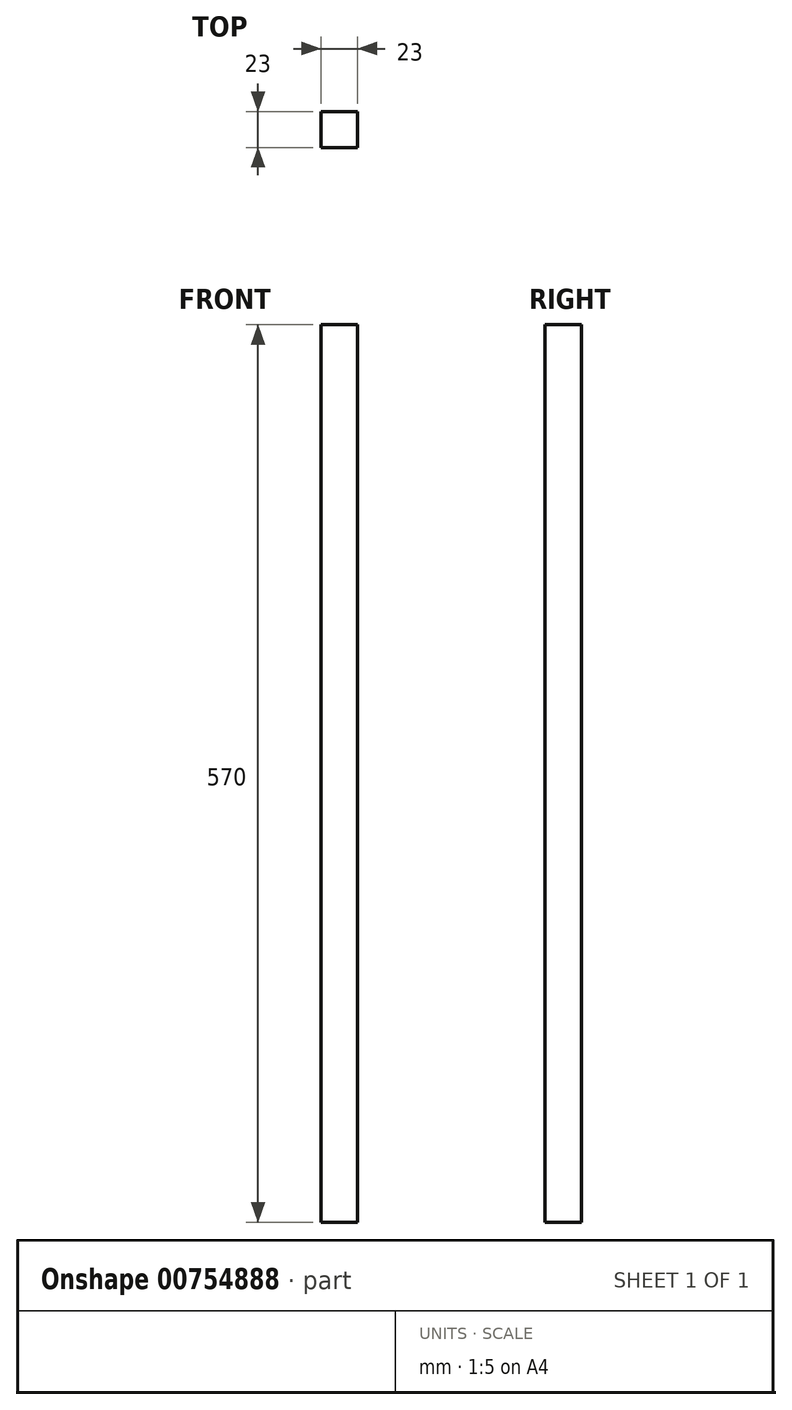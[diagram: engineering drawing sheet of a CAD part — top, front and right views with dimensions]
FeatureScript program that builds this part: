
annotation { "Feature Type Name" : "Feature", "Feature Type Description" : "" }
export const myFeature = defineFeature(function(context is Context, id is Id, definition is map)
    precondition{}
    {
        {
            var Q0;
            Q0=qCreatedBy(makeId("Top.planeOp"),FACE);
            var sketch = newSketch(context, id + "F0", { "sketchPlane" : qUnion([Q0])});
            skLineSegment(sketch, "E0.bottom", {"start": v(-11.5, 11.5) * mm, "end": v(11.5, 11.5) * mm});
            skLineSegment(sketch, "E0.top", {"start": v(-11.5, -11.5) * mm, "end": v(11.5, -11.5) * mm});
            skLineSegment(sketch, "E0.left", {"start": v(-11.5, 11.5) * mm, "end": v(-11.5, -11.5) * mm});
            skLineSegment(sketch, "E0.right", {"start": v(11.5, 11.5) * mm, "end": v(11.5, -11.5) * mm});
            skPoint(sketch, "E0.middle", {"position": v(0, 0) * mm});
            skSolve(sketch);
        }
        {
            var Q0;
            Q0=qSketchRegion(id+"F0",true);
            extrude(context, id + "F1", {"entities" : qUnion([Q0]), "depth" : 570 * mm, "offsetDistance" : 25 * mm});
        }
    });
